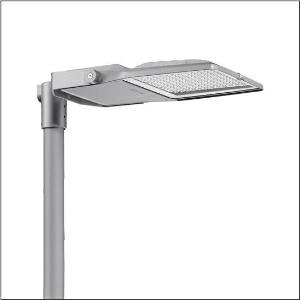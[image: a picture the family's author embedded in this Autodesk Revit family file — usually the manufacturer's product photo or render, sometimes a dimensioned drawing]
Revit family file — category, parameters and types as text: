
# Revit family: floodlight_fl_21_iq_midi___pl43_5xa7782f2a3a_db1b
name_source: partatom
category: Lighting Fixtures
units: mm (PartAtom-declared; Revit-internal decimal feet)

## family parameters
Cut with Voids When Loaded = No
Host = Face
Light Source = No
Part Type = Normal
Room Calculation Point = No
Round Connector Dimension = Use Diameter
Shared = No

## types (1)
- --- (1 x LED, 36680 lm, 270.2 W, 3000K)
    Apparent Load = 270 VA
    CIE Flux Codes = 27 78 99 100 100
    Color Rendering = 70
    Color Temperature = 3000K
    Default Elevation = 1800 mm
    Description = Floodlight FL 21 iQ midi, floodlight, primary light control with lens, of PMMA, primary optical cover: protective disc, of toughened safety glass, transparent, light distribution: PL43, light emission: direct distribution, installation type: surface-mounted, LED, High Power LED, rated luminous flux: 36.680lm, luminous efficacy: 136lm/W, light colour: 730, colour temperature: 3000K, control gear: ECG iQ, control: optimised constant luminous flux control (CLO 2.0), Desk-Remote (wireless, voltage-free reading and setting of iQ features in the workshop via application-optimized NFC function/RFID function), Smart-Wire, Night-Set, Temp-Guard, Auto-Match, Street-Remote, with terminal, 6-pole, mains connection: 220..240V, AC, 50/60Hz, start of lifetime: 270W, end of service life: 287W, reduction: 117W, luminaire housing, of diecast aluminium, powder-coated, Siteco® metallic grey (DB 702S), corrosivity category C5 mid according to DIN EN ISO 12944, sealing non-destructively replaceable, please order mast flange separately, mast bracket, of steel, galvanised, powder-coated, Siteco® metallic grey (DB 702S), protection rating (complete): IP66, insulation class (complete): insulation class II (safety insulation), certification: CE, ENEC, VDE, protection symbol: D, impact resistance: IK08, permissible operating ambient temperature: -40..+40°C, permissible operating ambient temperature for outdoor applications: -40..+50°C, standard: DIN EN 12944, LABS conformity tested according to VDMA 24364:2018-05, packaging unit: 1 piece

Light Distribution: PL43
    Height = 76 mm
    Lamp = 1 x LED
    Lamp Light Flux = 36680 lm
    Lamp Power = 270.2 W
    Lamp count = 1
    Length = 657 mm
    Luminous efficacy = 136 lm/W
    Manufacturer = Siteco
    ModVariant = No
    Model = 5XA7782F2A3A
    Number of Poles = 1
    OnlyDefault = Yes
    Power Factor = 1
    Product Name = Floodlight FL 21 iQ midi | PL43
    Product group = floodlight | pylon annexe
    ProductGroupID = 6200
    Protection Class = Protection class II
    Protection Degree = IP 66
    RLX_Detail_Level = 1
    RLX_Emergency_Light_Flux = 0 lm
    RLX_Emergency_Type = 0
    RLX_Emergency_Type_DB = No
    RlxData = <blob elided: 153425 chars, md5=e5bbfbfd>
    Socket = socket
    Standby Power = 0 W
    System Light Flux = 36680 lm
    System Power = 270 W
    Type Comments = factory setting: luminous flux: 100 % | dim-lin: 254 | 620 mA
    Type Image = l_1007123.jpg
    URL = http://relux.com
    VarID = @adj_073545
    Voltage = 0 V
    Weight = 0.00 kg
    Width = 442 mm

## geometry (parser evidence)
native form markers: Blend x4, Sweep x13
no freeform markers — native parametric forms only
